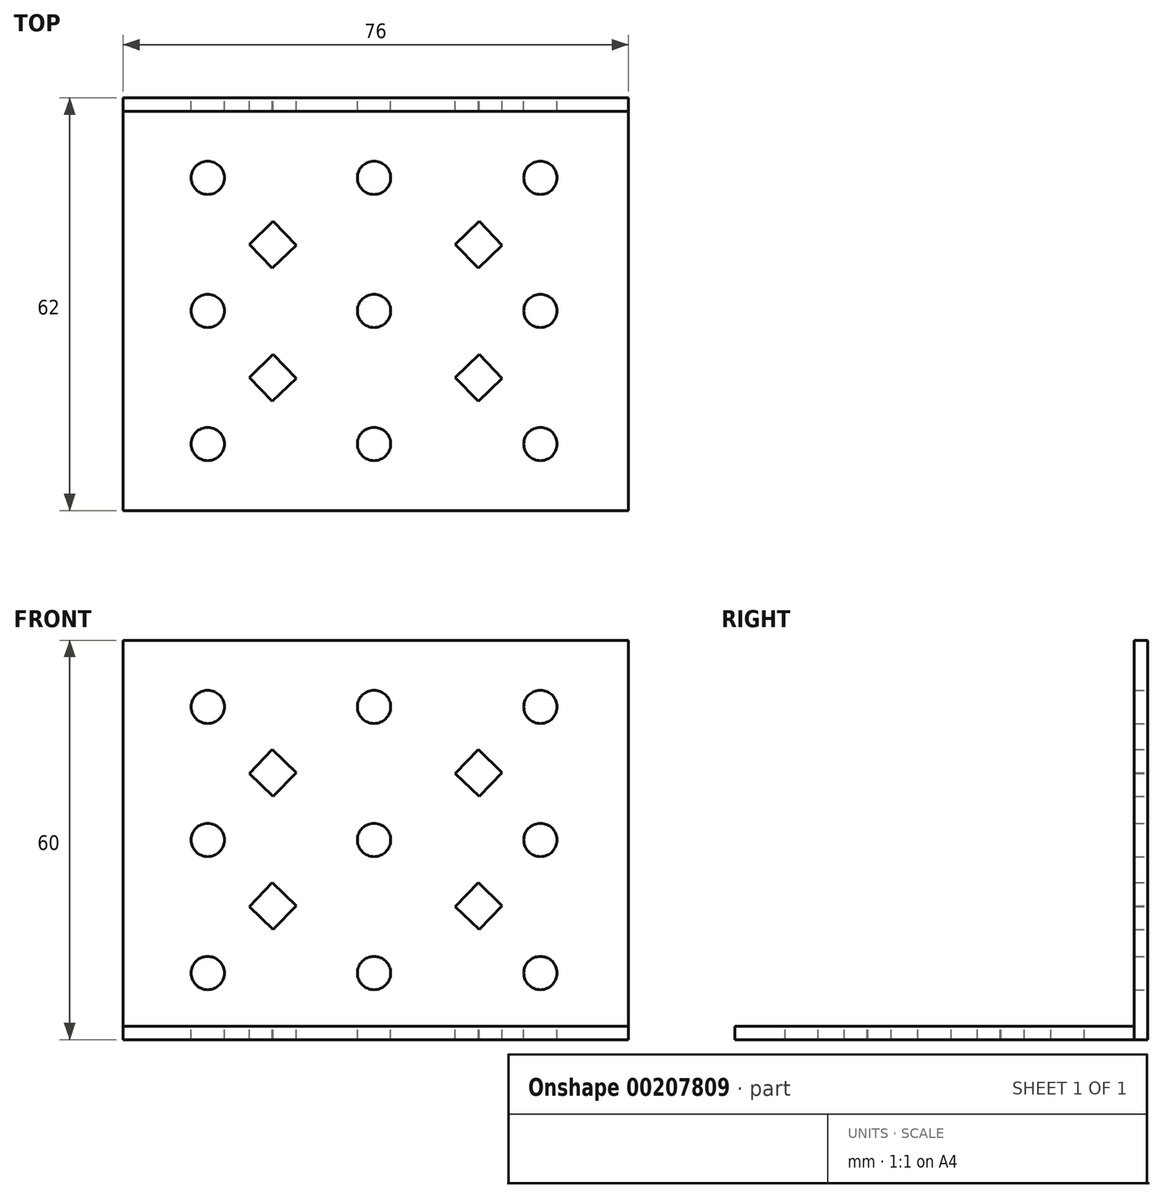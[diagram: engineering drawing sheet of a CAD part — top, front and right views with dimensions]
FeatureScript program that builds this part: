
annotation { "Feature Type Name" : "Feature", "Feature Type Description" : "" }
export const myFeature = defineFeature(function(context is Context, id is Id, definition is map)
    precondition{}
    {
        {
            assignVariable(context, id + "F0", {"name" : "PlateThickness", "anyValue" : 2 * mm});
        }
        {
            var Q0;
            Q0=qCreatedBy(makeId("Front.planeOp"),FACE);
            var sketch = newSketch(context, id + "F1", { "sketchPlane" : qUnion([Q0])});
            skLineSegment(sketch, "E0.bottom", {"start": v(-38, 0) * mm, "end": v(38, 0) * mm});
            skLineSegment(sketch, "E0.top", {"start": v(-38, 60) * mm, "end": v(38, 60) * mm});
            skLineSegment(sketch, "E0.left", {"start": v(-38, 0) * mm, "end": v(-38, 60) * mm});
            skLineSegment(sketch, "E0.right", {"start": v(38, 0) * mm, "end": v(38, 60) * mm});
            skCircle(sketch, "E1", {"center": v(-25.25, 50) * mm, "radius": 2.5 * mm});
            skLineSegment(sketch, "E2", {"start": v(-19, 40) * mm, "end": v(-15.53, 43.6) * mm});
            skLineSegment(sketch, "E3", {"start": v(-15.53, 43.6) * mm, "end": v(-11.93, 40.12) * mm});
            skLineSegment(sketch, "E4", {"start": v(-11.93, 40.12) * mm, "end": v(-15.4, 36.53) * mm});
            skLineSegment(sketch, "E5", {"start": v(-15.4, 36.53) * mm, "end": v(-19, 40) * mm});
            skCircle(sketch, "E6.0.1.0", {"center": v(-25.25, 30) * mm, "radius": 2.5 * mm});
            skCircle(sketch, "E6.0.2.0", {"center": v(-25.25, 10) * mm, "radius": 2.5 * mm});
            skCircle(sketch, "E6.1.0.0", {"center": v(-0.25, 50) * mm, "radius": 2.5 * mm});
            skCircle(sketch, "E6.1.1.0", {"center": v(-0.25, 30) * mm, "radius": 2.5 * mm});
            skCircle(sketch, "E6.1.2.0", {"center": v(-0.25, 10) * mm, "radius": 2.5 * mm});
            skLineSegment(sketch, "E6.direction1", {"start": v(-25.25, 50) * mm, "end": v(-0.25, 50) * mm, "construction": true});
            skLineSegment(sketch, "E6.direction2", {"start": v(-25.25, 50) * mm, "end": v(-25.25, 30) * mm, "construction": true});
            skCircle(sketch, "E7.0.2.0", {"center": v(24.75, 50) * mm, "radius": 2.5 * mm});
            skCircle(sketch, "E7.0.2.1", {"center": v(24.75, 30) * mm, "radius": 2.5 * mm});
            skCircle(sketch, "E7.0.2.2", {"center": v(24.75, 10) * mm, "radius": 2.5 * mm});
            skLineSegment(sketch, "E8.0.1.0", {"start": v(-11.93, 20.12) * mm, "end": v(-15.4, 16.53) * mm});
            skLineSegment(sketch, "E8.0.1.1", {"start": v(-15.4, 16.53) * mm, "end": v(-19, 20) * mm});
            skLineSegment(sketch, "E8.0.1.2", {"start": v(-15.53, 23.6) * mm, "end": v(-11.93, 20.12) * mm});
            skLineSegment(sketch, "E8.0.1.3", {"start": v(-19, 20) * mm, "end": v(-15.53, 23.6) * mm});
            skLineSegment(sketch, "E8.1.0.0", {"start": v(19, 40.12) * mm, "end": v(15.53, 36.53) * mm});
            skLineSegment(sketch, "E8.1.0.1", {"start": v(15.53, 36.53) * mm, "end": v(11.93, 40) * mm});
            skLineSegment(sketch, "E8.1.0.2", {"start": v(15.4, 43.6) * mm, "end": v(19, 40.12) * mm});
            skLineSegment(sketch, "E8.1.0.3", {"start": v(11.93, 40) * mm, "end": v(15.4, 43.6) * mm});
            skLineSegment(sketch, "E8.1.1.0", {"start": v(19, 20.12) * mm, "end": v(15.53, 16.53) * mm});
            skLineSegment(sketch, "E8.1.1.1", {"start": v(15.53, 16.53) * mm, "end": v(11.93, 20) * mm});
            skLineSegment(sketch, "E8.1.1.2", {"start": v(15.4, 23.6) * mm, "end": v(19, 20.12) * mm});
            skLineSegment(sketch, "E8.1.1.3", {"start": v(11.93, 20) * mm, "end": v(15.4, 23.6) * mm});
            skLineSegment(sketch, "E8.direction1", {"start": v(-19, 40) * mm, "end": v(11.93, 40) * mm, "construction": true});
            skLineSegment(sketch, "E8.direction2", {"start": v(-19, 40) * mm, "end": v(-19, 20) * mm, "construction": true});
            skSolve(sketch);
        }
        {
            var Q0;
            Q0 = qSketchRegion(id + "F1", true);
            extrude(context, id + "F2", {"entities" : qUnion([Q0]), "depth" : getVariable(context, 'PlateThickness')});
        }
        {
            var Q0;
            Q0=makeQuery(id+"F2.opExtrude","SWEPT_BODY",BODY,{"disambiguationData":[OSD([sQuery(id+"F1.wireOp",EDGE,"E0.bottom"),sQuery(id+"F1.wireOp",EDGE,"E0.top"),sQuery(id+"F1.wireOp",EDGE,"E0.left"),sQuery(id+"F1.wireOp",EDGE,"E0.right"),sQuery(id+"F1.wireOp",EDGE,"E1"),sQuery(id+"F1.wireOp",EDGE,"E2"),sQuery(id+"F1.wireOp",EDGE,"E3"),sQuery(id+"F1.wireOp",EDGE,"E4"),sQuery(id+"F1.wireOp",EDGE,"E5"),sQuery(id+"F1.wireOp",EDGE,"E6.0.1.0"),sQuery(id+"F1.wireOp",EDGE,"E6.0.2.0"),sQuery(id+"F1.wireOp",EDGE,"E6.1.0.0"),sQuery(id+"F1.wireOp",EDGE,"E6.1.1.0"),sQuery(id+"F1.wireOp",EDGE,"E6.1.2.0"),sQuery(id+"F1.wireOp",EDGE,"E7.0.2.0"),sQuery(id+"F1.wireOp",EDGE,"E7.0.2.1"),sQuery(id+"F1.wireOp",EDGE,"E7.0.2.2"),sQuery(id+"F1.wireOp",EDGE,"E8.0.1.0"),sQuery(id+"F1.wireOp",EDGE,"E8.0.1.1"),sQuery(id+"F1.wireOp",EDGE,"E8.0.1.2"),sQuery(id+"F1.wireOp",EDGE,"E8.0.1.3"),sQuery(id+"F1.wireOp",EDGE,"E8.1.0.0"),sQuery(id+"F1.wireOp",EDGE,"E8.1.0.1"),sQuery(id+"F1.wireOp",EDGE,"E8.1.0.2"),sQuery(id+"F1.wireOp",EDGE,"E8.1.0.3"),sQuery(id+"F1.wireOp",EDGE,"E8.1.1.0"),sQuery(id+"F1.wireOp",EDGE,"E8.1.1.1"),sQuery(id+"F1.wireOp",EDGE,"E8.1.1.2"),sQuery(id+"F1.wireOp",EDGE,"E8.1.1.3")])]});
            var Q1;
            Q1=makeQuery(id+"F2.opExtrude","CAP_EDGE",EDGE,{"disambiguationData":[OSD([sQuery(id+"F1.wireOp",EDGE,"E0.bottom")])],"isStart":false});
            transform(context, id + "F3", {"entities" : qUnion([Q0]), "transformType" : TransformType.ROTATION, "transformAxis" : qUnion([Q1]), "angle" : 90 * degree, "makeCopy" : true});
        }
    });
